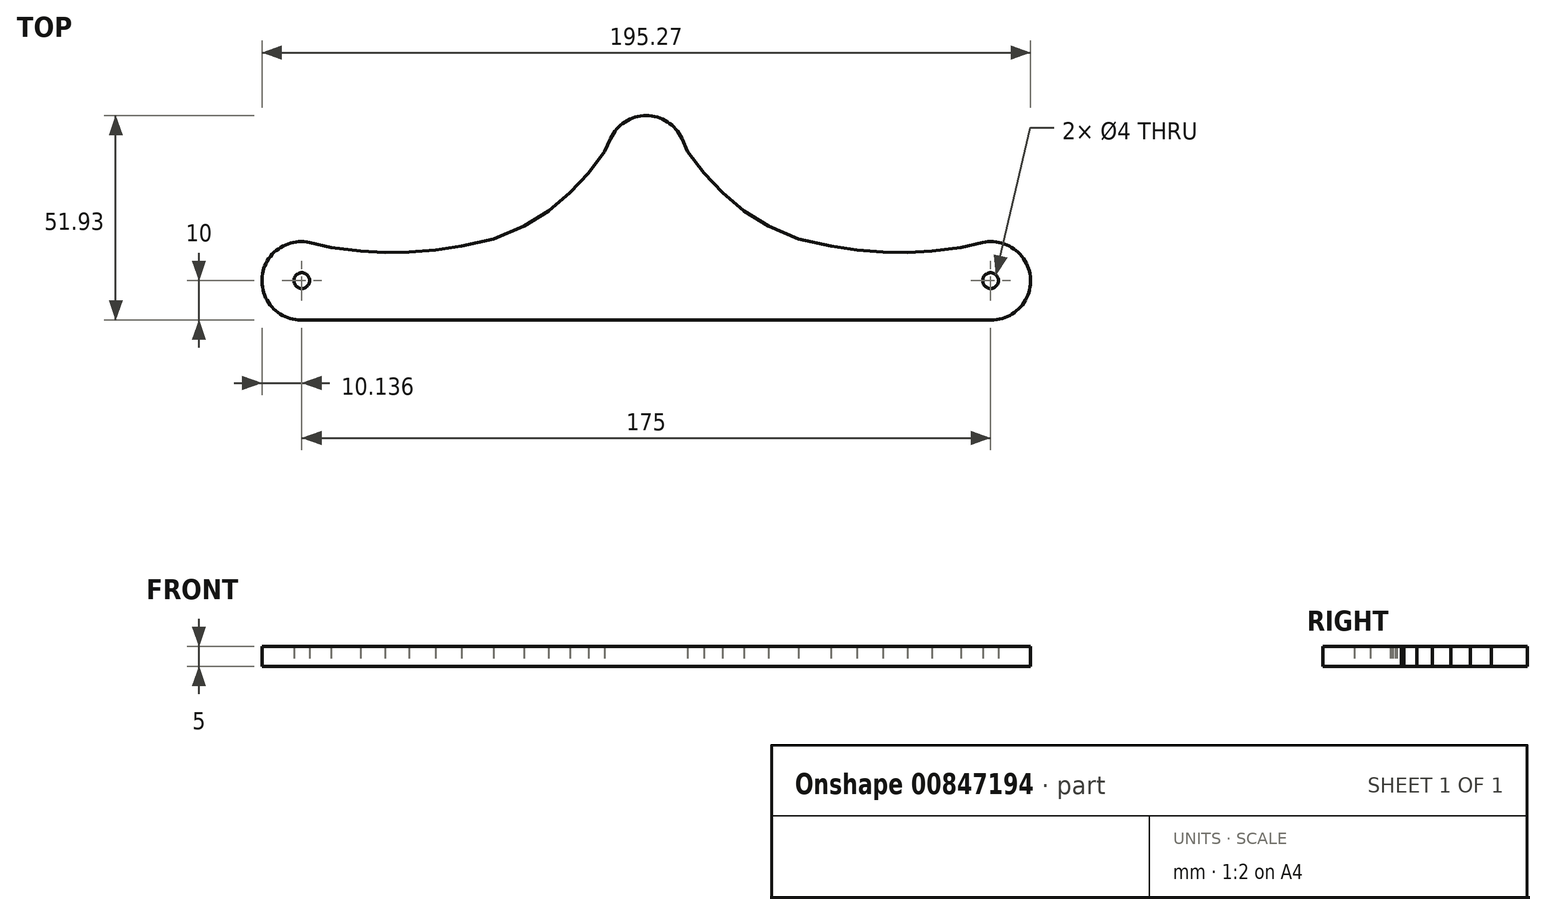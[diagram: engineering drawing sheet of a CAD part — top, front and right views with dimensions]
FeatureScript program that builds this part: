
annotation { "Feature Type Name" : "Feature", "Feature Type Description" : "" }
export const myFeature = defineFeature(function(context is Context, id is Id, definition is map)
    precondition{}
    {
        {
            var Q0;
            Q0=qCreatedBy(makeId("Top.planeOp"),FACE);
            var sketch = newSketch(context, id + "F0", { "sketchPlane" : qUnion([Q0])});
            skLineSegment(sketch, "E0", {"start": v(-89.14, -116.25) * mm, "end": v(86.24, -116.25) * mm});
            skLineSegment(sketch, "E1", {"start": v(-10.5, -70.19) * mm, "end": v(-12, -73.48) * mm});
            skLineSegment(sketch, "E2", {"start": v(-12, -73.48) * mm, "end": v(-16.1, -78.88) * mm});
            skLineSegment(sketch, "E3", {"start": v(-16.1, -78.88) * mm, "end": v(-20.78, -83.82) * mm});
            skLineSegment(sketch, "E4", {"start": v(-20.78, -83.82) * mm, "end": v(-26.33, -88.53) * mm});
            skLineSegment(sketch, "E5", {"start": v(-26.33, -88.53) * mm, "end": v(-32.46, -92.44) * mm});
            skLineSegment(sketch, "E6", {"start": v(-32.46, -92.44) * mm, "end": v(-40.2, -95.65) * mm});
            skLineSegment(sketch, "E7", {"start": v(-40.2, -95.65) * mm, "end": v(-48.36, -97.5) * mm});
            skLineSegment(sketch, "E8", {"start": v(-48.36, -97.5) * mm, "end": v(-54.98, -98.46) * mm});
            skLineSegment(sketch, "E9", {"start": v(-54.98, -98.46) * mm, "end": v(-61.65, -99) * mm});
            skLineSegment(sketch, "E10", {"start": v(-61.65, -99) * mm, "end": v(-67.85, -99.1) * mm});
            skLineSegment(sketch, "E11", {"start": v(-67.85, -99.1) * mm, "end": v(-74.04, -98.8) * mm});
            skLineSegment(sketch, "E12", {"start": v(-74.04, -98.8) * mm, "end": v(-81.45, -97.85) * mm});
            skLineSegment(sketch, "E13", {"start": v(-81.45, -97.85) * mm, "end": v(-86.92, -96.6) * mm});
            skCircle(sketch, "E14", {"center": v(-88.95, -106.25) * mm, "radius": 2 * mm});
            skLineSegment(sketch, "E15", {"start": v(7.59, -70.19) * mm, "end": v(9.08, -73.48) * mm});
            skLineSegment(sketch, "E16", {"start": v(9.08, -73.48) * mm, "end": v(13.2, -78.88) * mm});
            skLineSegment(sketch, "E17", {"start": v(13.2, -78.88) * mm, "end": v(17.87, -83.82) * mm});
            skLineSegment(sketch, "E18", {"start": v(17.87, -83.82) * mm, "end": v(23.42, -88.53) * mm});
            skLineSegment(sketch, "E19", {"start": v(23.42, -88.53) * mm, "end": v(29.55, -92.44) * mm});
            skLineSegment(sketch, "E20", {"start": v(29.55, -92.44) * mm, "end": v(37.29, -95.65) * mm});
            skLineSegment(sketch, "E21", {"start": v(37.29, -95.65) * mm, "end": v(45.45, -97.5) * mm});
            skLineSegment(sketch, "E22", {"start": v(45.45, -97.5) * mm, "end": v(52.07, -98.46) * mm});
            skLineSegment(sketch, "E23", {"start": v(52.07, -98.46) * mm, "end": v(58.74, -99) * mm});
            skLineSegment(sketch, "E24", {"start": v(58.74, -99) * mm, "end": v(64.94, -99.1) * mm});
            skLineSegment(sketch, "E25", {"start": v(64.94, -99.1) * mm, "end": v(71.13, -98.8) * mm});
            skLineSegment(sketch, "E26", {"start": v(71.13, -98.8) * mm, "end": v(78.55, -97.85) * mm});
            skLineSegment(sketch, "E27", {"start": v(78.55, -97.85) * mm, "end": v(84.02, -96.6) * mm});
            skCircle(sketch, "E28", {"center": v(86.05, -106.25) * mm, "radius": 2 * mm});
            skArc(sketch, "E29", {"start": v(-86.92, -96.6) * mm, "mid": v(-99.03, -105.18) * mm, "end": v(-89.14, -116.25) * mm});
            skArc(sketch, "E30", {"start": v(86.24, -116.25) * mm, "mid": v(96.12, -105.18) * mm, "end": v(84.02, -96.6) * mm});
            skArc(sketch, "E31", {"start": v(7.59, -70.19) * mm, "mid": v(-1.45, -64.32) * mm, "end": v(-10.5, -70.19) * mm});
            skSolve(sketch);
        }
        {
            var Q0;
            Q0 = qSketchRegion(id + "F0", true);
            extrude(context, id + "F1", {"entities" : qUnion([Q0]), "depth" : 5 * mm, "offsetDistance" : 25 * mm});
        }
    });
